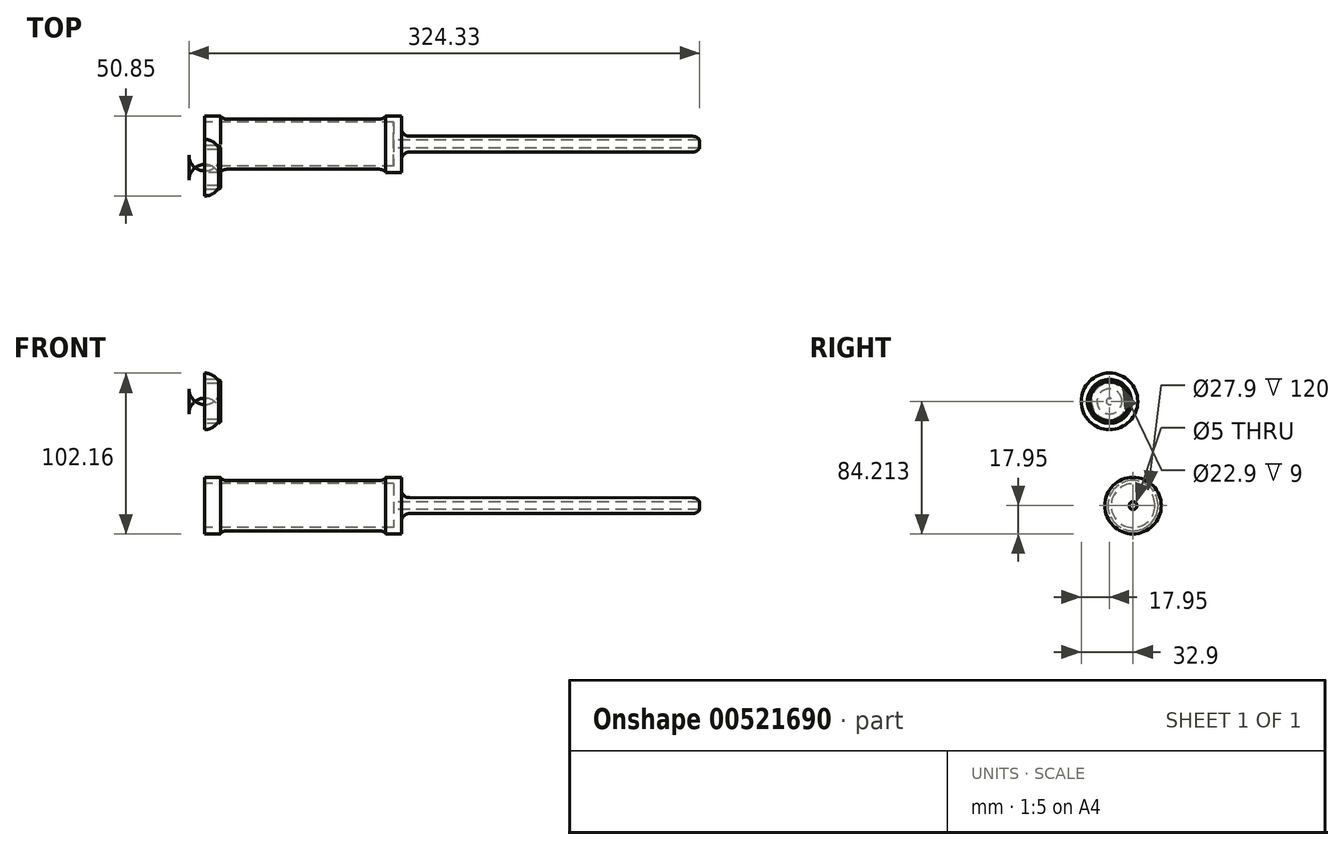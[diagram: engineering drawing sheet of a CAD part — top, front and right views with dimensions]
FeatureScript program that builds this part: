
annotation { "Feature Type Name" : "Feature", "Feature Type Description" : "" }
export const myFeature = defineFeature(function(context is Context, id is Id, definition is map)
    precondition{}
    {
        {
            var Q0;
            Q0=qCreatedBy(makeId("Top.planeOp"),FACE);
            var sketch = newSketch(context, id + "F0", { "sketchPlane" : qUnion([Q0])});
            skLineSegment(sketch, "E0", {"start": v(0, 32.9) * mm, "end": v(10, 32.9) * mm});
            skLineSegment(sketch, "E1", {"start": v(10, 32.9) * mm, "end": v(10, 30.9) * mm});
            skLineSegment(sketch, "E2", {"start": v(10, 30.9) * mm, "end": v(115, 30.9) * mm});
            skLineSegment(sketch, "E3", {"start": v(115, 30.9) * mm, "end": v(115, 32.9) * mm});
            skLineSegment(sketch, "E4", {"start": v(115, 32.9) * mm, "end": v(125, 32.9) * mm});
            skLineSegment(sketch, "E5", {"start": v(125, 14.95) * mm, "end": v(315, 14.95) * mm});
            skLineSegment(sketch, "E6", {"start": v(315, 14.95) * mm, "end": v(315, 19.95) * mm});
            skLineSegment(sketch, "E7", {"start": v(315, 19.95) * mm, "end": v(125, 20) * mm});
            skLineSegment(sketch, "E8", {"start": v(0, 32.9) * mm, "end": v(0, 14.95) * mm});
            skLineSegment(sketch, "E9", {"start": v(0, 14.95) * mm, "end": v(125, 14.95) * mm});
            skLineSegment(sketch, "E10", {"start": v(125, 32.9) * mm, "end": v(125, 20) * mm});
            skSolve(sketch);
        }
        {
            var Q0;
            Q0=qSketchRegion(id+"F0",true);
            var Q1;
            Q1=sQuery(id+"F0.wireOp",EDGE,"E9");
            revolve(context, id + "F1", {"entities" : qUnion([Q0]), "axis" : qUnion([Q1]), "revolveType" : RevolveType.FULL});
        }
        {
            var Q0;
            Q0=makeQuery(id+"F1.opRevolve","SWEPT_FACE",FACE,{"disambiguationData":[OSD([sQuery(id+"F0.wireOp",EDGE,"E2")])]});
            var Q1;
            Q1=makeQuery(id+"F1.opRevolve","SWEPT_FACE",FACE,{"disambiguationData":[OSD([sQuery(id+"F0.wireOp",EDGE,"E7")])]});
            fillet(context, id + "F2", {"entities" : qUnion([Q0, Q1]), "radius" : 5 * mm, "tangentPropagation" : true, "allowEdgeOverflow" : false});
        }
        {
            var Q0;
            Q0=makeQuery(id+"F1.opRevolve","SWEPT_FACE",FACE,{"disambiguationData":[OSD([sQuery(id+"F0.wireOp",EDGE,"E8")])]});
            var sketch = newSketch(context, id + "F3", { "sketchPlane" : qUnion([Q0])});
            skCircle(sketch, "E11", {"center": v(-14.95, 0) * mm, "radius": 13.95 * mm});
            skSolve(sketch);
        }
        {
            var Q0;
            Q0=qSketchRegion(id+"F3",true);
            extrude(context, id + "F4", {"entities" : qUnion([Q0]), "operationType" : NewBodyOperationType.REMOVE, "oppositeDirection" : true, "depth" : 120 * mm});
        }
        {
            var Q0;
            Q0=qCreatedBy(makeId("Right.planeOp"),FACE);
            var sketch = newSketch(context, id + "F5", { "sketchPlane" : qUnion([Q0])});
            skCircle(sketch, "E12", {"center": v(0, 66.26) * mm, "radius": 17.95 * mm});
            skSolve(sketch);
        }
        {
            var Q0;
            Q0=qSketchRegion(id+"F5",true);
            extrude(context, id + "F6", {"entities" : qUnion([Q0]), "oppositeDirection" : true, "depth" : 10 * mm});
        }
        {
            var Q0;
            Q0=makeQuery(id+"F6.opExtrude","CAP_FACE",FACE,{"disambiguationData":[OSD([sQuery(id+"F5.wireOp",EDGE,"E12")])],"isStart":true});
            var sketch = newSketch(context, id + "F7", { "sketchPlane" : qUnion([Q0])});
            skCircle(sketch, "E13", {"center": v(0, 66.26) * mm, "radius": 13.95 * mm});
            skCircle(sketch, "E14", {"center": v(0, 66.26) * mm, "radius": 11.45 * mm});
            skSolve(sketch);
        }
        {
            var Q0;
            Q0=makeQuery(id+"F7.imprint","IMPRINT",FACE,{"disambiguationData":[TD([[makeQuery(id+"F7.imprint","IMPRINT",EDGE,{"derivedFrom":sQuery(id+"F7.wireOp",EDGE,"E13")}),1.0]])]});
            var Q1;
            Q1=sQuery(id+"F7.wireOp",EDGE,"E14");
            var Q2;
            Q2=sQuery(id+"F7.wireOp",EDGE,"E13");
            extrude(context, id + "F8", {"entities" : qUnion([Q0]), "operationType" : NewBodyOperationType.ADD, "surfaceEntities" : qUnion([Q1, Q2]), "depth" : 10 * mm});
        }
        {
            var Q0;
            Q0=makeQuery(id+"F8.opExtrude","CAP_FACE",FACE,{"disambiguationData":[OSD([sQuery(id+"F7.wireOp",EDGE,"E13"),sQuery(id+"F7.wireOp",EDGE,"E14")])],"isStart":false});
            chamfer(context, id + "F9", {"entities" : qUnion([Q0]), "width" : 1 * mm, "tangentPropagation" : true});
        }
        {
            var Q0;
            Q0=makeQuery(id+"F6.opExtrude","CAP_EDGE",EDGE,{"disambiguationData":[OSD([sQuery(id+"F5.wireOp",EDGE,"E12")])],"isStart":false});
            fillet(context, id + "F10", {"entities" : qUnion([Q0]), "radius" : 10 * mm, "tangentPropagation" : true, "allowEdgeOverflow" : false});
        }
        {
            var Q0;
            Q0=makeQuery(id+"F4.boolean.opBoolean","COPY",FACE,{"derivedFrom":makeQuery(id+"F4.opExtrude","CAP_FACE",FACE,{"disambiguationData":[OSD([sQuery(id+"F3.wireOp",EDGE,"E11")])],"isStart":false})});
            var sketch = newSketch(context, id + "F11", { "sketchPlane" : qUnion([Q0])});
            skCircle(sketch, "E15", {"center": v(-14.95, 0) * mm, "radius": 2.5 * mm});
            skSolve(sketch);
        }
        {
            var Q0;
            Q0=makeQuery(id+"F11.imprint","IMPRINT",FACE,{"disambiguationData":[TD([[makeQuery(id+"F11.imprint","IMPRINT",EDGE,{"derivedFrom":sQuery(id+"F11.wireOp",EDGE,"E15")}),1.0]])]});
            var Q1;
            Q1=sQuery(id+"F11.wireOp",EDGE,"E15");
            extrude(context, id + "F12", {"entities" : qUnion([Q0]), "operationType" : NewBodyOperationType.REMOVE, "surfaceEntities" : qUnion([Q1]), "endBound" : BoundingType.THROUGH_ALL, "oppositeDirection" : true, "depth" : 25 * mm});
        }
    });
